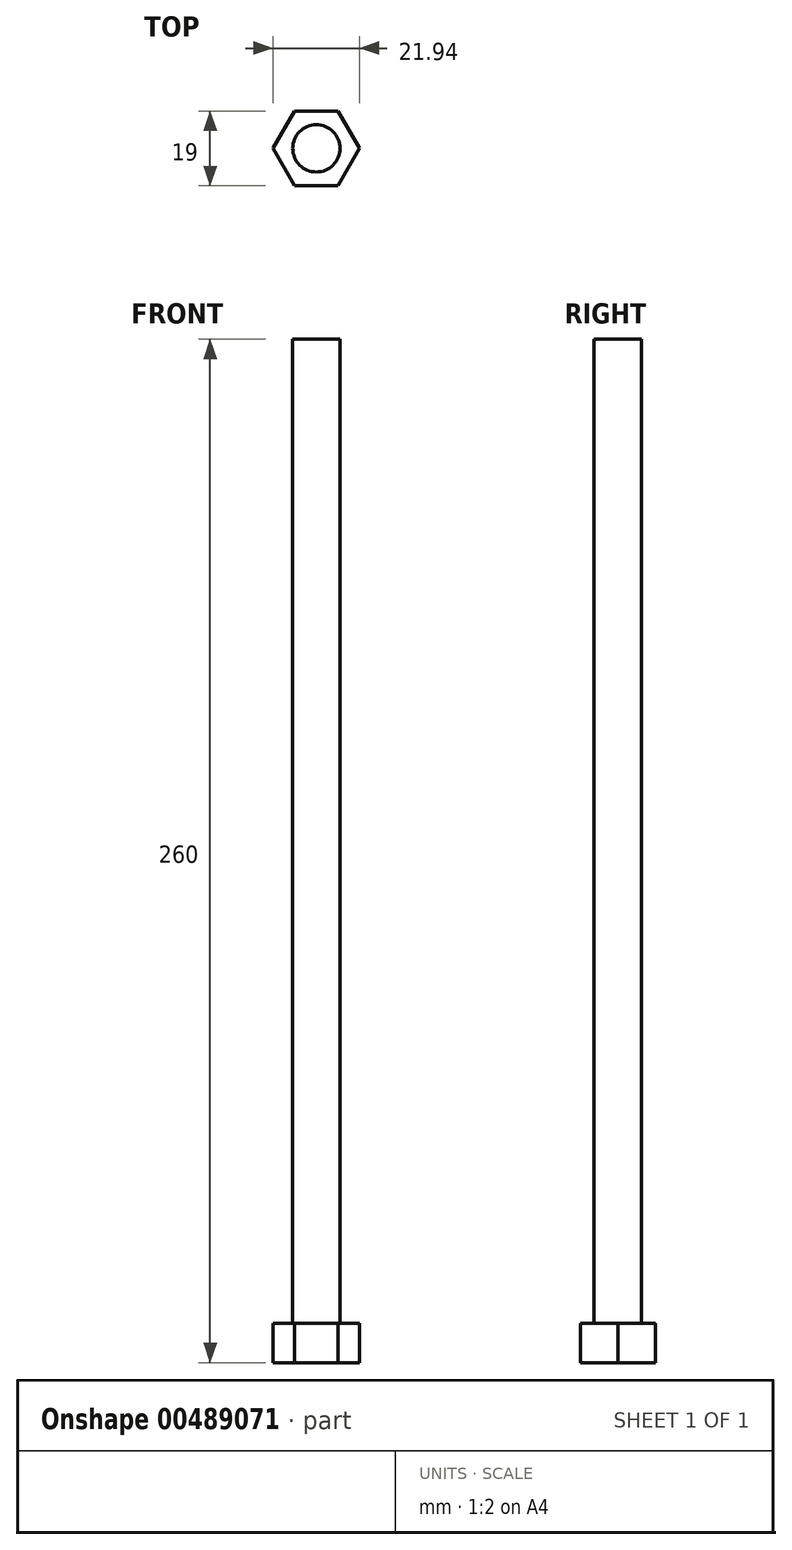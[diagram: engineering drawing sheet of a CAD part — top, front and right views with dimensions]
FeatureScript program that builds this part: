
annotation { "Feature Type Name" : "Feature", "Feature Type Description" : "" }
export const myFeature = defineFeature(function(context is Context, id is Id, definition is map)
    precondition{}
    {
        {
            var Q0;
            Q0=qCreatedBy(makeId("Top.planeOp"),FACE);
            var sketch = newSketch(context, id + "F0", { "sketchPlane" : qUnion([Q0])});
            skCircle(sketch, "E0", {"center": v(0, 0) * mm, "radius": 9.5 * mm, "construction": true});
            skLineSegment(sketch, "E1", {"start": v(5.48, 9.5) * mm, "end": v(10.97, 0) * mm});
            skLineSegment(sketch, "E2", {"start": v(-10.97, 0) * mm, "end": v(-5.48, 9.5) * mm});
            skLineSegment(sketch, "E3", {"start": v(-5.48, 9.5) * mm, "end": v(5.48, 9.5) * mm});
            skLineSegment(sketch, "E4.1.0", {"start": v(10.97, 0) * mm, "end": v(5.48, -9.5) * mm});
            skLineSegment(sketch, "E4.1.1", {"start": v(5.48, -9.5) * mm, "end": v(-5.48, -9.5) * mm});
            skLineSegment(sketch, "E4.1.2", {"start": v(-5.48, -9.5) * mm, "end": v(-10.97, 0) * mm});
            skSolve(sketch);
        }
        {
            var Q0;
            Q0=makeQuery(id+"F0.imprint","IMPRINT",FACE,{"disambiguationData":[TD([[makeQuery(id+"F0.imprint","IMPRINT",EDGE,{"derivedFrom":sQuery(id+"F0.wireOp",EDGE,"E1")}),-1.0]])]});
            extrude(context, id + "F1", {"entities" : qUnion([Q0]), "depth" : 10 * mm});
        }
        {
            var Q0;
            Q0=makeQuery(id+"F1.opExtrude","CAP_FACE",FACE,{"disambiguationData":[OSD([sQuery(id+"F0.wireOp",EDGE,"E1"),sQuery(id+"F0.wireOp",EDGE,"E2"),sQuery(id+"F0.wireOp",EDGE,"E3"),sQuery(id+"F0.wireOp",EDGE,"E4.1.0"),sQuery(id+"F0.wireOp",EDGE,"E4.1.1"),sQuery(id+"F0.wireOp",EDGE,"E4.1.2")])],"isStart":false});
            var sketch = newSketch(context, id + "F2", { "sketchPlane" : qUnion([Q0])});
            skCircle(sketch, "E5", {"center": v(0, 0) * mm, "radius": 6 * mm});
            skSolve(sketch);
        }
        {
            var Q0;
            Q0 = qSketchRegion(id + "F2", true);
            extrude(context, id + "F3", {"entities" : qUnion([Q0]), "operationType" : NewBodyOperationType.ADD, "depth" : 250 * mm});
        }
    });
